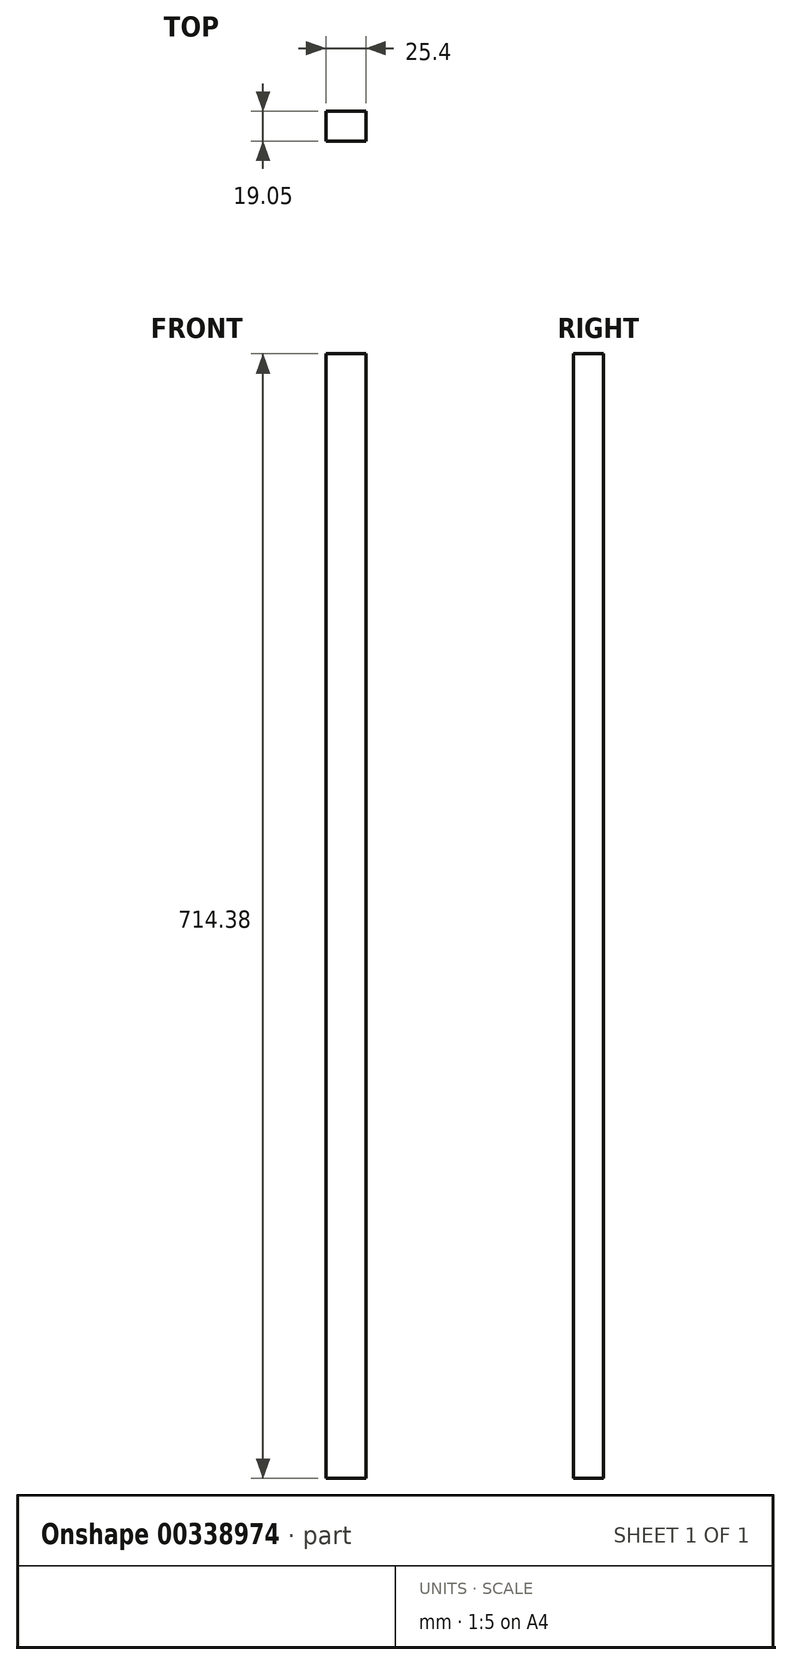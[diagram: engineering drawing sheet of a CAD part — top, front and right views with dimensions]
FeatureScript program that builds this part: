
annotation { "Feature Type Name" : "Feature", "Feature Type Description" : "" }
export const myFeature = defineFeature(function(context is Context, id is Id, definition is map)
    precondition{}
    {
        {
            var Q0;
            Q0=qCreatedBy(makeId("Front.planeOp"),FACE);
            var sketch = newSketch(context, id + "F0", { "sketchPlane" : qUnion([Q0])});
            skLineSegment(sketch, "E0.bottom", {"start": v(12.7, -357.19) * mm, "end": v(-12.7, -357.19) * mm});
            skLineSegment(sketch, "E0.top", {"start": v(12.7, 357.19) * mm, "end": v(-12.7, 357.19) * mm});
            skLineSegment(sketch, "E0.left", {"start": v(12.7, -357.19) * mm, "end": v(12.7, 357.19) * mm});
            skLineSegment(sketch, "E0.right", {"start": v(-12.7, -357.19) * mm, "end": v(-12.7, 357.19) * mm});
            skPoint(sketch, "E0.middle", {"position": v(0, 0) * mm});
            skSolve(sketch);
        }
        {
            var Q0;
            Q0 = qSketchRegion(id + "F0", true);
            extrude(context, id + "F1", {"entities" : qUnion([Q0]), "depth" : 19.05 * mm});
        }
    });
